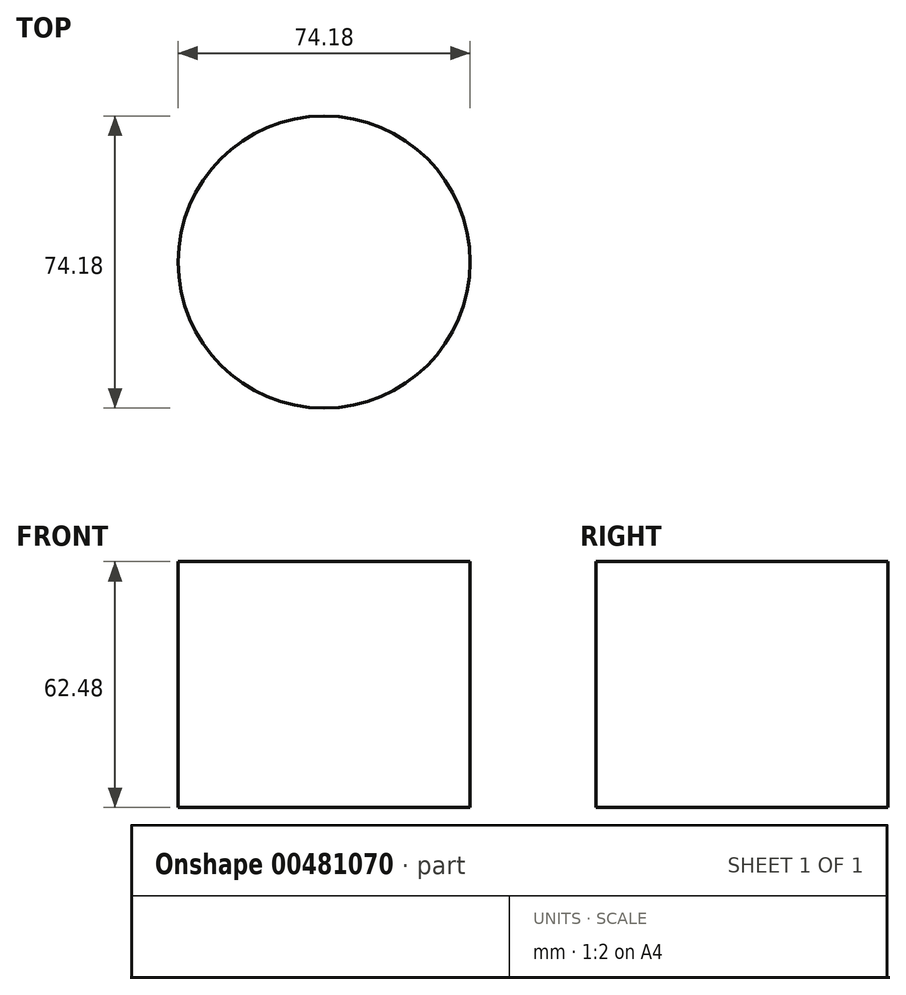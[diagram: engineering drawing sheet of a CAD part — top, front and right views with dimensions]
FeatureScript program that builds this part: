
annotation { "Feature Type Name" : "Feature", "Feature Type Description" : "" }
export const myFeature = defineFeature(function(context is Context, id is Id, definition is map)
    precondition{}
    {
        {
            var Q0;
            Q0=qCreatedBy(makeId("Top.planeOp"),FACE);
            var sketch = newSketch(context, id + "F0", { "sketchPlane" : qUnion([Q0])});
            skCircle(sketch, "E0", {"center": v(0, 0) * mm, "radius": 37.1 * mm});
            skSolve(sketch);
        }
        {
            var Q0;
            Q0 = qSketchRegion(id + "F0", true);
            extrude(context, id + "F1", {"entities" : qUnion([Q0]), "oppositeDirection" : true, "depth" : 62.48 * mm});
        }
    });
